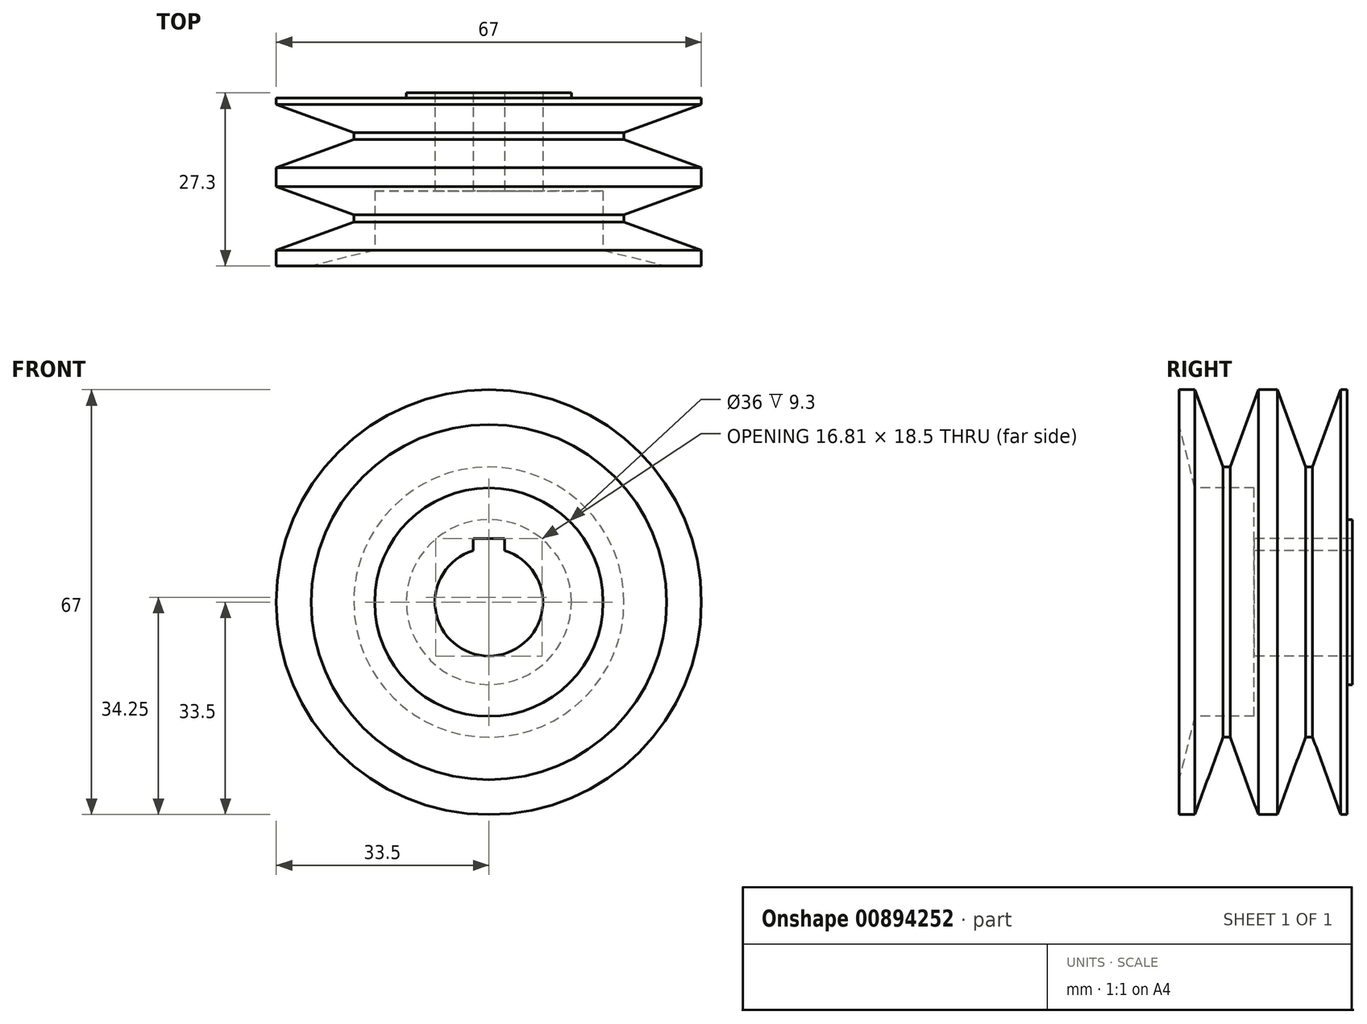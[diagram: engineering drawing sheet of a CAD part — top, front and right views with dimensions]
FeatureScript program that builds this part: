
annotation { "Feature Type Name" : "Feature", "Feature Type Description" : "" }
export const myFeature = defineFeature(function(context is Context, id is Id, definition is map)
    precondition{}
    {
        {
            var Q0;
            Q0=qCreatedBy(makeId("Right.planeOp"),FACE);
            var sketch = newSketch(context, id + "F0", { "sketchPlane" : qUnion([Q0])});
            skLineSegment(sketch, "E0", {"start": v(0, 33.5) * mm, "end": v(0, 28) * mm});
            skLineSegment(sketch, "E1", {"start": v(0, 0) * mm, "end": v(27.3, 0) * mm});
            skLineSegment(sketch, "E2", {"start": v(0, 33.5) * mm, "end": v(2.5, 33.5) * mm});
            skLineSegment(sketch, "E3", {"start": v(27.3, 8.5) * mm, "end": v(27.3, 13) * mm});
            skLineSegment(sketch, "E4", {"start": v(26.5, 13) * mm, "end": v(26.5, 33.5) * mm});
            skLineSegment(sketch, "E5", {"start": v(27.3, 13) * mm, "end": v(26.5, 13) * mm});
            skLineSegment(sketch, "E6", {"start": v(26.5, 33.5) * mm, "end": v(25.5, 33.5) * mm});
            skLineSegment(sketch, "E7", {"start": v(12.5, 33.5) * mm, "end": v(15.5, 33.5) * mm});
            skLineSegment(sketch, "E8", {"start": v(2.5, 33.5) * mm, "end": v(6.94, 21.3) * mm});
            skLineSegment(sketch, "E9", {"start": v(12.5, 33.5) * mm, "end": v(8.06, 21.3) * mm});
            skLineSegment(sketch, "E10", {"start": v(15.5, 33.5) * mm, "end": v(19.94, 21.3) * mm});
            skLineSegment(sketch, "E11", {"start": v(25.5, 33.5) * mm, "end": v(21.06, 21.3) * mm});
            skLineSegment(sketch, "E12", {"start": v(21.06, 21.3) * mm, "end": v(19.94, 21.3) * mm});
            skLineSegment(sketch, "E13", {"start": v(8.06, 21.3) * mm, "end": v(6.94, 21.3) * mm});
            skLineSegment(sketch, "E14", {"start": v(27.3, 8.5) * mm, "end": v(11.8, 8.5) * mm});
            skLineSegment(sketch, "E15", {"start": v(11.8, 18) * mm, "end": v(11.8, 8.5) * mm});
            skLineSegment(sketch, "E16", {"start": v(11.8, 18) * mm, "end": v(2.5, 18) * mm});
            skLineSegment(sketch, "E17", {"start": v(0, 28) * mm, "end": v(2.5, 18) * mm});
            skLineSegment(sketch, "E18", {"start": v(0, 28) * mm, "end": v(0, 0) * mm, "construction": true});
            skSolve(sketch);
        }
        {
            var Q0;
            Q0 = qSketchRegion(id + "F0", true);
            var Q1;
            Q1=sQuery(id+"F0.wireOp",EDGE,"E1");
            revolve(context, id + "F1", {"surfaceOperationType" : NewSurfaceOperationType.NEW, "entities" : qUnion([Q0]), "axis" : qUnion([Q1]), "revolveType" : RevolveType.FULL});
        }
        {
            var Q0;
            Q0=qCreatedBy(makeId("Front.planeOp"),FACE);
            var sketch = newSketch(context, id + "F2", { "sketchPlane" : qUnion([Q0])});
            skLineSegment(sketch, "E19.bottom", {"start": v(-2.5, 7) * mm, "end": v(2.5, 7) * mm});
            skLineSegment(sketch, "E19.top", {"start": v(-2.5, 10) * mm, "end": v(2.5, 10) * mm});
            skLineSegment(sketch, "E19.left", {"start": v(-2.5, 7) * mm, "end": v(-2.5, 10) * mm});
            skLineSegment(sketch, "E19.right", {"start": v(2.5, 7) * mm, "end": v(2.5, 10) * mm});
            skLineSegment(sketch, "E20", {"start": v(0, 7) * mm, "end": v(0, 0) * mm, "construction": true});
            skSolve(sketch);
        }
        {
            var Q0;
            Q0 = qSketchRegion(id + "F2", true);
            extrude(context, id + "F3", {"entities" : qUnion([Q0]), "operationType" : NewBodyOperationType.REMOVE, "endBound" : BoundingType.THROUGH_ALL, "oppositeDirection" : true, "depth" : 25 * mm, "offsetDistance" : 25 * mm});
        }
    });
